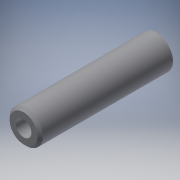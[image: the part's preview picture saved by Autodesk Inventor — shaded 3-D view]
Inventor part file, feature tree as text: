
AUTODESK INVENTOR PART (.ipt)
format: ipt  version: 2016 (Build 200138000, 138)  size: 96,768 bytes
history: native  units: mm
features: extrude x1, chamfer x1, sketch x1
ambient origin geometry x8: Origin, YZ Plane, XZ Plane, XY Plane, X Axis, Y Axis, Z Axis, Center Point
bodies: Solid1 (feature_tree)
feature tree (3):
  extrude  "Extrusion1"  Depth=2.0mm
  chamfer  "Chamfer1"  Distance=200.0mm
  sketch  "Sketch1"  dims[d0=50.0mm d1=23.5mm d2=200.0mm d3=0.0mm d4=4.0mm d5=2.0mm d6=45.0deg]
